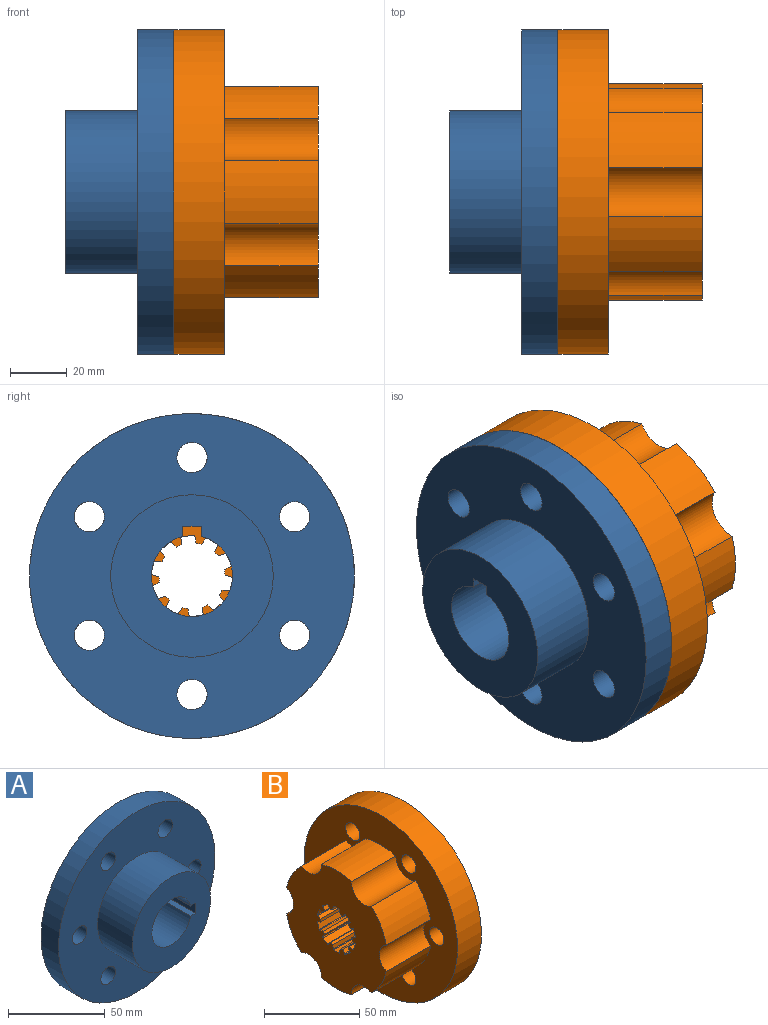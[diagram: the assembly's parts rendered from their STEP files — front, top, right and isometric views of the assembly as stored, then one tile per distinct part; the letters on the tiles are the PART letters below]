
ASSEMBLY  parts=2 mates=1
PART A: 17 faces, bbox 114.3x49x114.3 mm
  f0: plane 60.58x60.58mm, normal (0,1,0), area 2220.1mm2, adj f5,f7,f8,f9,f10
  f1: plane 57.15x57.15mm, normal (0,-1,0), area 1903mm2, adj f6,f7,f8,f9,f10
  f2: cylinder r=57.15mm len=114.3mm, axis (0,1,0), area 4560.4mm2, adj f3,f4
  f3: plane 114.3x114.3mm, normal (0,-1,0), area 7159.3mm2, adj f2,f6,f11,f12,f13,f14,f15,f16
  f4: plane 114.3x114.3mm, normal (0,1,0), area 6842.3mm2, adj f2,f5,f11,f12,f13,f14,f15,f16
  f5: cylinder r=30.29mm len=60.58mm, axis (0,-1,0), area 2078.6mm2, adj f0,f4
  f6: cylinder r=28.57mm len=57.15mm, axis (0,1,0), area 4560.4mm2, adj f1,f3
  f7: cylinder r=14.29mm len=49.02mm, axis (0,1,0), area 4086.8mm2, adj f0,f1,f8,f10
  f8: plane 49.02x3.53mm, normal (0,0,-1), area 173.2mm2, adj f0,f1,f7,f9
  f9: plane 49.02x6.35mm, normal (-1,0,0), area 311.3mm2, adj f0,f1,f8,f10
  f10: plane 49.02x3.53mm, normal (0,0,1), area 173.2mm2, adj f0,f1,f7,f9
  f11: cylinder r=5.33mm len=12.7mm, axis (0,1,0), area 425.6mm2, adj f3,f4
  f12: cylinder r=5.33mm len=12.7mm, axis (0,1,0), area 425.6mm2, adj f3,f4
  f13: cylinder r=5.33mm len=12.7mm, axis (0,1,0), area 425.6mm2, adj f3,f4
  f14: cylinder r=5.33mm len=12.7mm, axis (0,1,0), area 425.6mm2, adj f3,f4
  f15: cylinder r=5.33mm len=12.7mm, axis (0,1,0), area 425.6mm2, adj f3,f4
  f16: cylinder r=5.33mm len=12.7mm, axis (0,1,0), area 425.6mm2, adj f3,f4
PART B: 84 faces, bbox 50.8x114.3x114.3 mm
  f0: cylinder r=38.1mm len=33.02mm, axis (-1,0,0), area 750.3mm2, adj f12,f77,f81,f82
  f1: cylinder r=38.1mm len=33.02mm, axis (-1,0,0), area 750.3mm2, adj f12,f77,f80,f81
  f2: cylinder r=38.1mm len=33.02mm, axis (-1,0,0), area 750.3mm2, adj f12,f77,f79,f80
  f3: cylinder r=38.1mm len=33.02mm, axis (-1,0,0), area 750.3mm2, adj f12,f77,f78,f79
  f4: cylinder r=38.1mm len=33.02mm, axis (-1,0,0), area 750.3mm2, adj f12,f77,f78,f83
  f5: cylinder r=38.1mm len=33.02mm, axis (-1,0,0), area 750.3mm2, adj f12,f77,f82,f83
  f6: cylinder r=5.33mm len=17.78mm, axis (1,0,0), area 595.9mm2, adj f25,f77
  f7: cylinder r=5.33mm len=17.78mm, axis (1,0,0), area 595.9mm2, adj f25,f77
  f8: cylinder r=5.33mm len=17.78mm, axis (1,0,0), area 595.9mm2, adj f25,f77
  f9: cylinder r=5.33mm len=17.78mm, axis (1,0,0), area 595.9mm2, adj f25,f77
  f10: cylinder r=5.33mm len=17.78mm, axis (1,0,0), area 595.9mm2, adj f25,f77
  f11: cylinder r=5.33mm len=17.78mm, axis (1,0,0), area 595.9mm2, adj f25,f77
  f12: plane 76.2x74.27mm, normal (-1,0,0), area 3565.8mm2, adj f0,f1,f2,f3,f4,f5,f15,f16
  f13: cylinder r=57.15mm len=114.3mm, axis (-1,0,0), area 6384.5mm2, adj f25,f77
  f14: plane 63.5x63.5mm, normal (1,0,0), area 2610mm2, adj f15,f16,f17,f18,f19,f20,f21,f22
  f15: cylinder r=11.62mm len=38.1mm, axis (1,0,0), area 73.1mm2, adj f12,f14,f29,f56
  f16: cylinder r=11.62mm len=38.1mm, axis (1,0,0), area 73.1mm2, adj f12,f14,f55,f58
  f17: cylinder r=11.62mm len=38.1mm, axis (1,0,0), area 73.1mm2, adj f12,f14,f52,f53
  f18: cylinder r=11.62mm len=38.1mm, axis (1,0,0), area 73.1mm2, adj f12,f14,f49,f50
  f19: cylinder r=11.62mm len=38.1mm, axis (1,0,0), area 73.1mm2, adj f12,f14,f46,f47
  f20: cylinder r=11.62mm len=38.1mm, axis (1,0,0), area 73.1mm2, adj f12,f14,f41,f42
  f21: cylinder r=11.62mm len=38.1mm, axis (1,0,0), area 73.1mm2, adj f12,f14,f38,f39
  f22: cylinder r=11.62mm len=38.1mm, axis (1,0,0), area 73.1mm2, adj f12,f14,f35,f36
  f23: cylinder r=11.62mm len=38.1mm, axis (1,0,0), area 73.1mm2, adj f12,f14,f32,f33
  f24: cylinder r=31.75mm len=63.5mm, axis (-1,0,0), area 2533.5mm2, adj f14,f25
  f25: plane 114.3x114.3mm, normal (1,0,0), area 6557.6mm2, adj f6,f7,f8,f9,f10,f11,f13,f24
  f26: cylinder r=11.62mm len=38.1mm, axis (1,0,0), area 73.1mm2, adj f12,f14,f28,f30
  f27: plane 38.1x3.9mm, normal (0,0,1), area 148.5mm2, adj f12,f14,f75,f76
  f28: plane 38.1x2.39mm, normal (0,1,0.09), area 91.3mm2, adj f12,f14,f26,f75
  f29: plane 38.1x2.39mm, normal (0,-1,0.09), area 91.3mm2, adj f12,f14,f15,f76
  f30: plane 38.1x1.81mm, normal (0,-0.75,0.66), area 91.3mm2, adj f12,f14,f26,f74
  f31: plane 38.1x3.15mm, normal (0,0.59,0.81), area 148.5mm2, adj f12,f14,f73,f74
  f32: plane 38.1x2.06mm, normal (0,0.86,-0.51), area 91.3mm2, adj f12,f14,f23,f73
  f33: plane 38.1x2.34mm, normal (0,-0.22,0.97), area 91.3mm2, adj f12,f14,f23,f72
  f34: plane 38.1x3.71mm, normal (0,0.95,0.31), area 148.5mm2, adj f12,f14,f71,f72
  f35: plane 38.1x2.2mm, normal (0,0.39,-0.92), area 91.3mm2, adj f12,f14,f22,f71
  f36: plane 38.1x2.2mm, normal (0,0.39,0.92), area 91.3mm2, adj f12,f14,f22,f70
  f37: plane 38.1x3.71mm, normal (0,0.95,-0.31), area 148.5mm2, adj f12,f14,f69,f70
  f38: plane 38.1x2.34mm, normal (0,-0.22,-0.97), area 91.3mm2, adj f12,f14,f21,f69
  f39: plane 38.1x2.06mm, normal (0,0.86,0.51), area 91.3mm2, adj f12,f14,f21,f68
  f40: plane 38.1x3.15mm, normal (0,0.59,-0.81), area 148.5mm2, adj f12,f14,f67,f68
  f41: plane 38.1x1.81mm, normal (0,-0.75,-0.66), area 91.3mm2, adj f12,f14,f20,f67
  f42: plane 38.1x2.19mm, normal (0,1,-0.09), area 83.6mm2, adj f12,f14,f20,f43
  f43: cylinder r=0.73mm len=38.1mm, axis (1,0,0), area 41.2mm2, adj f12,f14,f42,f44
  f44: plane 38.1x3.49mm, normal (0,0,-1), area 133mm2, adj f12,f14,f43,f45
  f45: cylinder r=0.73mm len=38.1mm, axis (1,0,0), area 41.2mm2, adj f12,f14,f44,f46
  f46: plane 38.1x2.19mm, normal (0,-1,-0.09), area 83.6mm2, adj f12,f14,f19,f45
  f47: plane 38.1x1.81mm, normal (0,0.75,-0.66), area 91.3mm2, adj f12,f14,f19,f66
  f48: plane 38.1x3.15mm, normal (0,-0.59,-0.81), area 148.5mm2, adj f12,f14,f65,f66
  f49: plane 38.1x2.06mm, normal (0,-0.86,0.51), area 91.3mm2, adj f12,f14,f18,f65
  f50: plane 38.1x2.34mm, normal (0,0.22,-0.97), area 91.3mm2, adj f12,f14,f18,f64
  f51: plane 38.1x3.71mm, normal (0,-0.95,-0.31), area 148.5mm2, adj f12,f14,f63,f64
  f52: plane 38.1x2.2mm, normal (0,-0.39,0.92), area 91.3mm2, adj f12,f14,f17,f63
  f53: plane 38.1x2.2mm, normal (0,-0.39,-0.92), area 91.3mm2, adj f12,f14,f17,f62
  f54: plane 38.1x3.71mm, normal (0,-0.95,0.31), area 148.5mm2, adj f12,f14,f61,f62
  f55: plane 38.1x2.34mm, normal (0,0.22,0.97), area 91.3mm2, adj f12,f14,f16,f61
  f56: plane 38.1x1.81mm, normal (0,0.75,0.66), area 91.3mm2, adj f12,f14,f15,f59
  f57: plane 38.1x3.15mm, normal (0,-0.59,0.81), area 148.5mm2, adj f12,f14,f59,f60
  f58: plane 38.1x2.06mm, normal (0,-0.86,-0.51), area 91.3mm2, adj f12,f14,f16,f60
  f59: cylinder r=0.51mm len=38.1mm, axis (-1,0,0), area 28.7mm2, adj f12,f14,f56,f57
  f60: cylinder r=0.51mm len=38.1mm, axis (1,0,0), area 28.7mm2, adj f12,f14,f57,f58
  f61: cylinder r=0.51mm len=38.1mm, axis (-1,0,0), area 28.7mm2, adj f12,f14,f54,f55
  f62: cylinder r=0.51mm len=38.1mm, axis (1,0,0), area 28.7mm2, adj f12,f14,f53,f54
  f63: cylinder r=0.51mm len=38.1mm, axis (-1,0,0), area 28.7mm2, adj f12,f14,f51,f52
  f64: cylinder r=0.51mm len=38.1mm, axis (1,0,0), area 28.7mm2, adj f12,f14,f50,f51
  f65: cylinder r=0.51mm len=38.1mm, axis (-1,0,0), area 28.7mm2, adj f12,f14,f48,f49
  f66: cylinder r=0.51mm len=38.1mm, axis (1,0,0), area 28.7mm2, adj f12,f14,f47,f48
  f67: cylinder r=0.51mm len=38.1mm, axis (-1,0,0), area 28.7mm2, adj f12,f14,f40,f41
  f68: cylinder r=0.51mm len=38.1mm, axis (1,0,0), area 28.7mm2, adj f12,f14,f39,f40
  f69: cylinder r=0.51mm len=38.1mm, axis (-1,0,0), area 28.7mm2, adj f12,f14,f37,f38
  f70: cylinder r=0.51mm len=38.1mm, axis (1,0,0), area 28.7mm2, adj f12,f14,f36,f37
  f71: cylinder r=0.51mm len=38.1mm, axis (-1,0,0), area 28.7mm2, adj f12,f14,f34,f35
  f72: cylinder r=0.51mm len=38.1mm, axis (1,0,0), area 28.7mm2, adj f12,f14,f33,f34
  f73: cylinder r=0.51mm len=38.1mm, axis (-1,0,0), area 28.7mm2, adj f12,f14,f31,f32
  f74: cylinder r=0.51mm len=38.1mm, axis (1,0,0), area 28.7mm2, adj f12,f14,f30,f31
  f75: cylinder r=0.51mm len=38.1mm, axis (-1,0,0), area 28.7mm2, adj f12,f14,f27,f28
  f76: cylinder r=0.51mm len=38.1mm, axis (1,0,0), area 28.7mm2, adj f12,f14,f27,f29
  f77: plane 114.3x114.3mm, normal (-1,0,0), area 5601.7mm2, adj f0,f1,f2,f3,f4,f5,f6,f7
  f78: cylinder r=9.65mm len=33.02mm, axis (1,0,0), area 688.7mm2, adj f3,f4,f12,f77
  f79: cylinder r=9.65mm len=33.02mm, axis (1,0,0), area 688.7mm2, adj f2,f3,f12,f77
  f80: cylinder r=9.65mm len=33.02mm, axis (1,0,0), area 688.7mm2, adj f1,f2,f12,f77
  f81: cylinder r=9.65mm len=33.02mm, axis (1,0,0), area 688.7mm2, adj f0,f1,f12,f77
  f82: cylinder r=9.65mm len=33.02mm, axis (1,0,0), area 688.7mm2, adj f0,f5,f12,f77
  f83: cylinder r=9.65mm len=33.02mm, axis (1,0,0), area 688.7mm2, adj f4,f5,f12,f77
PLACE A rot(axis=(-0.58,-0.58,-0.58),120deg) t=(-15.36,-11.66,-9.88)mm
PLACE B rot(axis=(0,-0.97,-0.26),180deg) t=(-2.66,-11.66,-9.88)mm
MATE revolute B.f13 <-> A.f2  axis (-1,0,0) through (-15.36,-11.66,-9.88)mm
